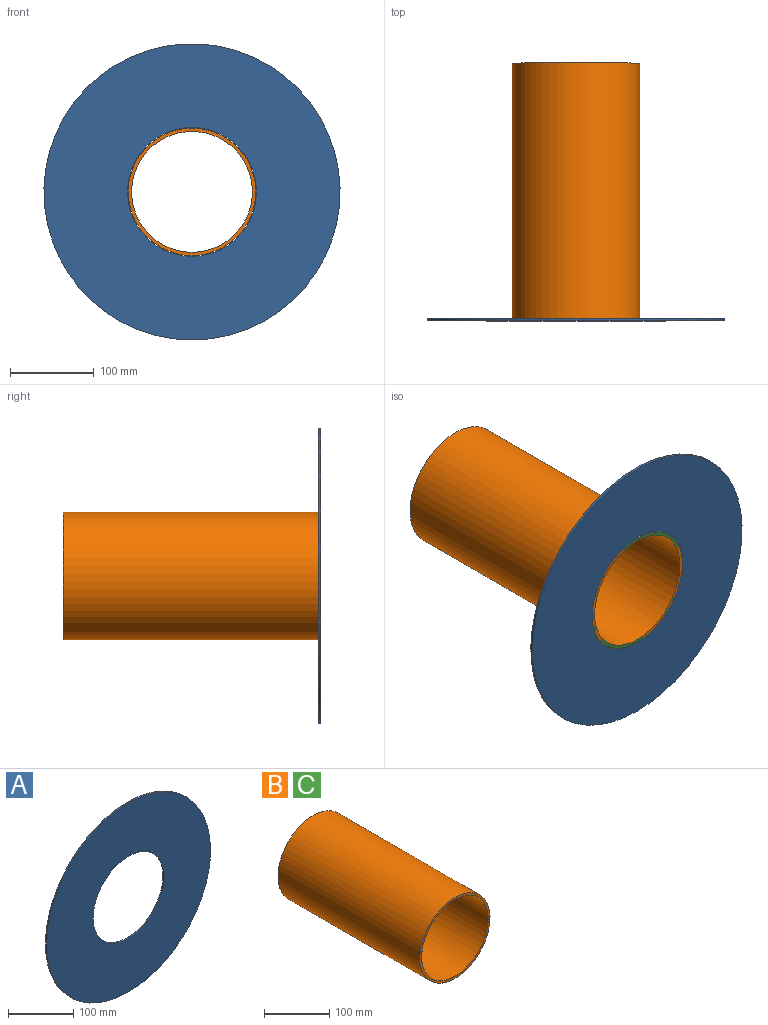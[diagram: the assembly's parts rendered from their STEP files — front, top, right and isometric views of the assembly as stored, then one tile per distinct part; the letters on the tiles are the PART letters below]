
ASSEMBLY  parts=3 mates=1
PART A: 4 faces, bbox 354x3x354 mm
  f0: cylinder r=77mm len=154mm, axis (0,1,0), area 1451.4mm2, adj f2,f3
  f1: cylinder r=177mm len=354mm, axis (0,1,0), area 3336.4mm2, adj f2,f3
  f2: plane 354x354mm, normal (0,-1,0), area 79796.5mm2, adj f0,f1
  f3: plane 354x354mm, normal (0,1,0), area 79796.5mm2, adj f0,f1
PART B: 4 faces, bbox 152.4x308x152.4 mm
  f0: cylinder r=72.2mm len=308mm, axis (0,1,0), area 139723mm2, adj f2,f3
  f1: cylinder r=76.2mm len=308mm, axis (0,1,0), area 147463.8mm2, adj f2,f3
  f2: plane 152.4x152.4mm, normal (0,-1,0), area 1864.8mm2, adj f0,f1
  f3: plane 152.4x152.4mm, normal (0,1,0), area 1864.8mm2, adj f0,f1
PART C: same geometry as B
PLACE A t=(0,-305,0)mm
PLACE B at identity
PLACE C at identity
MATE fastened A.f0 <-> B.f1  axis (0,-1,0) through (0,-308,0)mm
